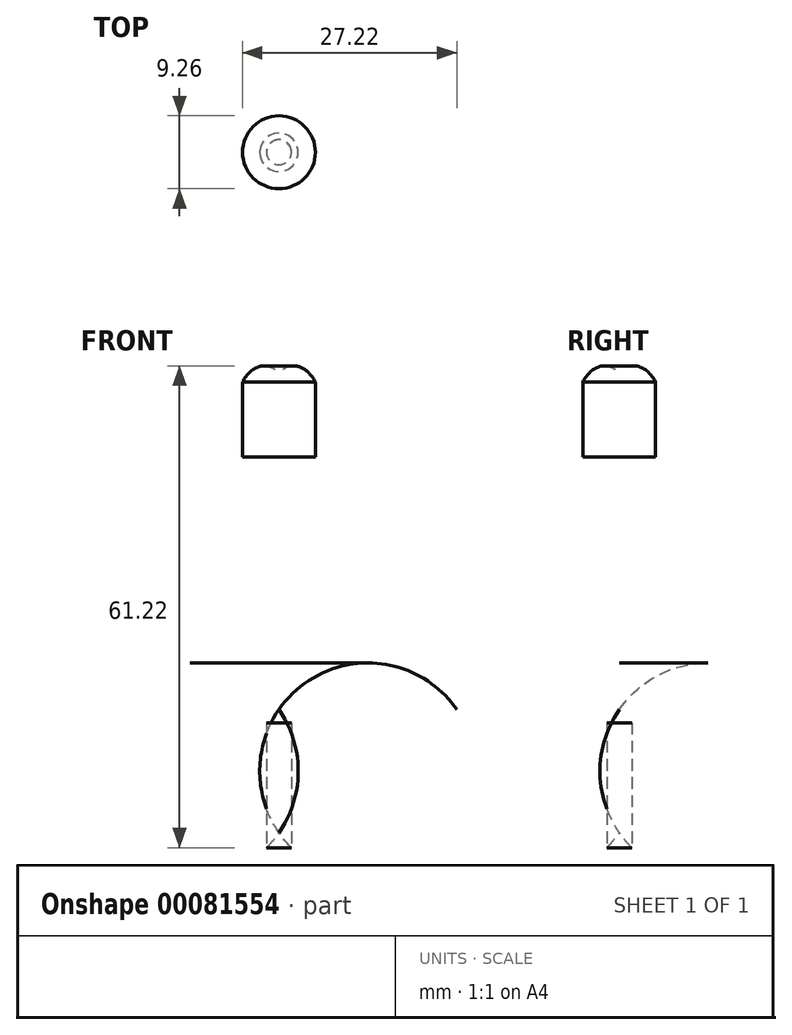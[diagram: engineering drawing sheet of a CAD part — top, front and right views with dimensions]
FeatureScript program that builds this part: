
annotation { "Feature Type Name" : "Feature", "Feature Type Description" : "" }
export const myFeature = defineFeature(function(context is Context, id is Id, definition is map)
    precondition{}
    {
        {
            var Q0;
            Q0=qCreatedBy(makeId("Front.planeOp"),FACE);
            var sketch = newSketch(context, id + "F0", { "sketchPlane" : qUnion([Q0])});
            skLineSegment(sketch, "E0", {"start": v(0, -8.3) * mm, "end": v(0, 50.12) * mm});
            skFitSpline(sketch, "E1", {"points": [v(0, -8.3) * mm, v(18.4, -8.3) * mm, v(20.57, 14.56) * mm, v(15.85, 13.79) * mm, v(6.62, 17.7) * mm, v(5.23, 47.58) * mm, v(0, 50.12) * mm, v(0, -8.3) * mm]});
            skLineSegment(sketch, "E2", {"start": v(4.63, 48.99) * mm, "end": v(4.63, 39.46) * mm});
            skLineSegment(sketch, "E3", {"start": v(4.63, 39.46) * mm, "end": v(0, 39.46) * mm});
            skLineSegment(sketch, "E4", {"start": v(0, 39.46) * mm, "end": v(0, 50.12) * mm});
            skLineSegment(sketch, "E5", {"start": v(1.59, -10.2) * mm, "end": v(1.59, 5.68) * mm});
            skLineSegment(sketch, "E6", {"start": v(1.59, 5.68) * mm, "end": v(0, 5.68) * mm});
            skLineSegment(sketch, "E7", {"start": v(0, 5.68) * mm, "end": v(0, -8.3) * mm});
            skLineSegment(sketch, "E8", {"start": v(8.67, -13.38) * mm, "end": v(8.67, -13.38) * mm});
            skPoint(sketch, "E9.start.orphan", {"position": v(-22.56, 56.6) * mm});
            skPoint(sketch, "E10.end.orphan", {"position": v(-44.13, -13.38) * mm});
            skPoint(sketch, "E10.start.orphan", {"position": v(-44.13, 56.6) * mm});
            skPoint(sketch, "E11.orphan", {"position": v(-42.32, -13.38) * mm});
            skPoint(sketch, "E12.start.orphan", {"position": v(-34.72, 56.6) * mm});
            skPoint(sketch, "E13.end.orphan", {"position": v(-34.72, -12.94) * mm});
            skPoint(sketch, "E13.start.orphan", {"position": v(-34.72, -13.38) * mm});
            skLineSegment(sketch, "E14", {"start": v(-32.13, 56.63) * mm, "end": v(-34.72, 56.6) * mm});
            skLineSegment(sketch, "E15", {"start": v(8.75, -13.38) * mm, "end": v(8.75, -13.38) * mm});
            skSolve(sketch);
        }
        {
            var Q0;
            Q0=makeQuery(id+"F0.imprint","IMPRINT",FACE,{"disambiguationData":[TD([[makeQuery(id+"F0.imprint","IMPRINT",EDGE,{"derivedFrom":sQuery(id+"F0.wireOp",EDGE,"E0")}),-1.0]])]});
            var Q1;
            Q1=sQuery(id+"F0.wireOp",EDGE,"E0");
            revolve(context, id + "F1", {"entities" : qUnion([Q0]), "axis" : qUnion([Q1]), "revolveType" : RevolveType.FULL});
        }
    });
